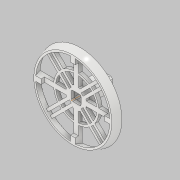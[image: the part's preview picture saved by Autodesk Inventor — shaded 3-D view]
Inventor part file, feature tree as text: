
AUTODESK INVENTOR PART (.ipt)
format: ipt  version: 2019.2 (Build 232265000, 265)  size: 1,720,320 bytes
history: native  units: mm
features: extrude x6, sketch x6, other x5, chamfer x4, plane x3, fillet x2, shell x1, revolve x1, delete_face x1, projected_geometry x1
ambient origin geometry x8: Origin, YZ Plane, XZ Plane, XY Plane, X Axis, Y Axis, Z Axis, Center Point
bodies: Volumenkörper1 (feature_tree), Volumenkörper2 (feature_tree)
feature tree (30):
  other  "BaseTop.ipt"
  shell  "ShellLower.ipt"  Thickness=10.0mm
  extrude  "Extrusion3"  Depth=3.0mm
  extrude  "Extrusion2"  Depth=1.5mm
  chamfer  "Fase2"  Distance=2.0mm Angle=45.0deg
  fillet  "Rundung1"  Radius=2.0mm
  extrude  "Extrusion5"  Depth=10.0mm
  sketch  "Skizze7"  dims[d31=2.5mm d32=7.0mm]
  extrude  "Extrusion6"  Depth=7.0mm
  extrude  "Extrusion7"  Depth=4.0mm
  chamfer  "Fase3"  Distance=40.0mm Angle=360.0deg
  chamfer  "Fase4"  Distance=40.0mm Angle=360.0deg
  plane  "Arbeitsebene5"
  other  "Arbeitsachse2"
  revolve  "Umdrehung2"
  plane  "Arbeitsebene6"
  other  "Trennen3"
  plane  "Arbeitsebene7"
  other  "Trennen4"
  other  "Kombinieren1"
  delete_face  "Fläche löschen1"
  extrude  "Extrusion8"  Depth=3.0mm
  chamfer  "Fase5"  Distance=5.0mm
  fillet  "Rundung2"  Radius=5.0mm
  sketch  "Skizze2"  dims[d6=35.0mm d7=0.0mm d11=3.0mm]
  sketch  "Skizze3"  dims[d12=3.0mm d13=0.0mm d14=1.5mm d15=2.8mm d16=2.0mm d17=45.0deg d28=2.0mm]
  sketch  "Skizze6"  dims[d29=10.0mm d30=120.0mm]
  projected_geometry  "Projizierte Kontur1"
  sketch  "Skizze8"  dims[d33=7.0mm d35=4.0mm d36=40.0mm d38=360.0deg d40=40.0mm d42=360.0deg]
  sketch  "Skizze9"  dims[d44=60.0mm d45=3.0mm d46=5.0mm d47=0.0mm d48=5.0mm d49=0.0mm d50=5.0mm d51=0.0mm d52=3.0mm d53=2.0mm d54=45.0deg d55=1.0mm d56=2.0mm d57=45.0deg d58=-20.5mm d59=119.5mm d60=2.5mm d61=180.0deg d62=14.5mm d63=11.0mm d64=10.0mm d65=40.0mm d67=360.0deg d69=5.0mm d70=0.0mm d71=1.0mm d72=2.0mm d73=45.0deg d74=0.25mm]
